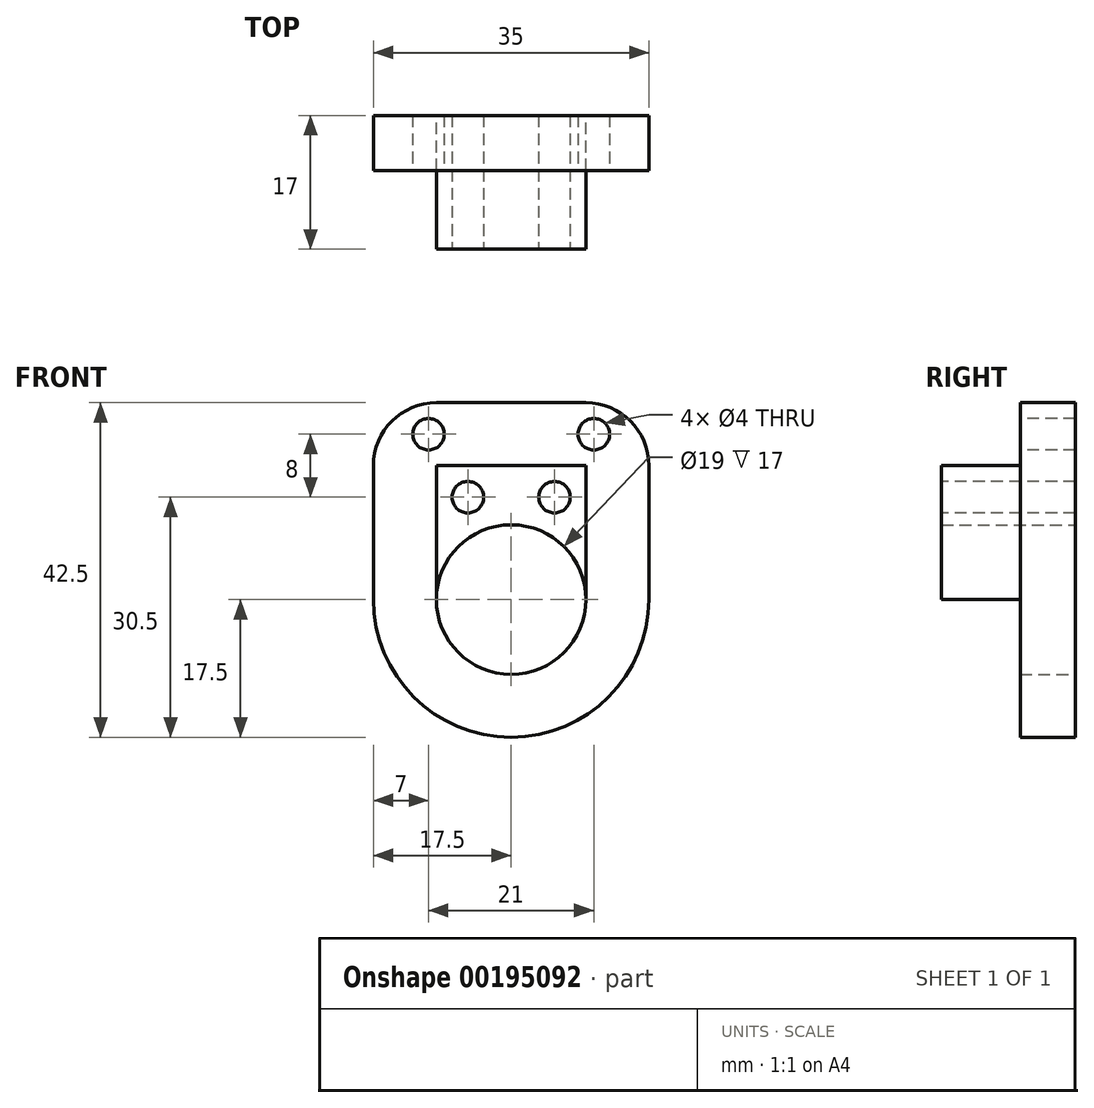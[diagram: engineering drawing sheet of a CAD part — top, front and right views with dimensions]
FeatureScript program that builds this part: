
annotation { "Feature Type Name" : "Feature", "Feature Type Description" : "" }
export const myFeature = defineFeature(function(context is Context, id is Id, definition is map)
    precondition{}
    {
        {
            var Q0;
            Q0=qCreatedBy(makeId("Front.planeOp"),FACE);
            var sketch = newSketch(context, id + "F0", { "sketchPlane" : qUnion([Q0])});
            skCircle(sketch, "E0", {"center": v(0, 0) * mm, "radius": 9.5 * mm});
            skArc(sketch, "E1", {"start": v(-17.5, 0) * mm, "mid": v(0, -17.5) * mm, "end": v(17.5, 0) * mm});
            skLineSegment(sketch, "E2", {"start": v(17.5, 0) * mm, "end": v(17.5, 25) * mm});
            skLineSegment(sketch, "E3", {"start": v(17.5, 25) * mm, "end": v(-17.5, 25) * mm});
            skLineSegment(sketch, "E4", {"start": v(-17.5, 25) * mm, "end": v(-17.5, 0) * mm});
            skSolve(sketch);
        }
        {
            var Q0;
            Q0 = qSketchRegion(id + "F0", true);
            extrude(context, id + "F1", {"entities" : qUnion([Q0]), "depth" : 7 * mm});
        }
        {
            var Q0;
            Q0=makeQuery(id+"F1.opExtrude","CAP_FACE",FACE,{"disambiguationData":[OSD([sQuery(id+"F0.wireOp",EDGE,"E0"),sQuery(id+"F0.wireOp",EDGE,"E1"),sQuery(id+"F0.wireOp",EDGE,"E2"),sQuery(id+"F0.wireOp",EDGE,"E3"),sQuery(id+"F0.wireOp",EDGE,"E4")])],"isStart":false});
            var sketch = newSketch(context, id + "F2", { "sketchPlane" : qUnion([Q0])});
            skArc(sketch, "E5.0", {"start": v(9.5, 0) * mm, "mid": v(0, 9.5) * mm, "end": v(-9.5, 0) * mm});
            skLineSegment(sketch, "E6", {"start": v(9.5, 0) * mm, "end": v(9.5, 17) * mm});
            skLineSegment(sketch, "E7", {"start": v(-9.5, 17) * mm, "end": v(-9.5, 0) * mm});
            skLineSegment(sketch, "E8", {"start": v(9.5, 17) * mm, "end": v(-9.5, 17) * mm});
            skSolve(sketch);
        }
        {
            var Q0;
            Q0 = qSketchRegion(id + "F2", true);
            extrude(context, id + "F3", {"entities" : qUnion([Q0]), "operationType" : NewBodyOperationType.ADD, "depth" : 10 * mm});
        }
        {
            var Q0;
            Q0=makeQuery(id+"F1.opExtrude","CAP_FACE",FACE,{"disambiguationData":[OSD([sQuery(id+"F0.wireOp",EDGE,"E0"),sQuery(id+"F0.wireOp",EDGE,"E1"),sQuery(id+"F0.wireOp",EDGE,"E2"),sQuery(id+"F0.wireOp",EDGE,"E3"),sQuery(id+"F0.wireOp",EDGE,"E4")])],"isStart":false});
            var sketch = newSketch(context, id + "F4", { "sketchPlane" : qUnion([Q0])});
            skPoint(sketch, "E9", {"position": v(-10.5, 21) * mm});
            skPoint(sketch, "E10", {"position": v(10.5, 21) * mm});
            skSolve(sketch);
        }
        {
            var Q0;
            Q0=sQuery(id+"F4.wireOp",VERTEX,"E9");
            var Q1;
            Q1=sQuery(id+"F4.wireOp",VERTEX,"E10");
            var Q2;
            Q2=makeQuery(id+"F1.opExtrude","SWEPT_BODY",BODY,{"disambiguationData":[OSD([sQuery(id+"F0.wireOp",EDGE,"E0"),sQuery(id+"F0.wireOp",EDGE,"E1"),sQuery(id+"F0.wireOp",EDGE,"E2"),sQuery(id+"F0.wireOp",EDGE,"E3"),sQuery(id+"F0.wireOp",EDGE,"E4")])]});
            hole(context, id + "F5", {"style" : HoleStyle.SIMPLE, "endStyle" : HoleEndStyle.BLIND, "holeDiameter" : 4 * mm, "holeDepth" : 10 * mm, "locations" : qUnion([Q0, Q1]), "scope" : qUnion([Q2])});
        }
        {
            var Q0;
            Q0=makeQuery(id+"F3.opExtrude","CAP_FACE",FACE,{"disambiguationData":[OSD([sQuery(id+"F2.wireOp",EDGE,"E5.0"),sQuery(id+"F2.wireOp",EDGE,"E6"),sQuery(id+"F2.wireOp",EDGE,"E7"),sQuery(id+"F2.wireOp",EDGE,"E8")])],"isStart":false});
            var sketch = newSketch(context, id + "F6", { "sketchPlane" : qUnion([Q0])});
            skPoint(sketch, "E11", {"position": v(-5.5, 13) * mm});
            skPoint(sketch, "E12", {"position": v(5.5, 13) * mm});
            skLineSegment(sketch, "E13", {"start": v(0, 17) * mm, "end": v(0, 3.41) * mm, "construction": true});
            skPoint(sketch, "E13.endSnap0", {"position": v(0, 9.5) * mm});
            skSolve(sketch);
        }
        {
            var Q0;
            Q0=sQuery(id+"F6.wireOp",VERTEX,"E11");
            var Q1;
            Q1=sQuery(id+"F6.wireOp",VERTEX,"E12");
            var Q2;
            Q2=makeQuery(id+"F1.opExtrude","SWEPT_BODY",BODY,{"disambiguationData":[OSD([sQuery(id+"F0.wireOp",EDGE,"E0"),sQuery(id+"F0.wireOp",EDGE,"E1"),sQuery(id+"F0.wireOp",EDGE,"E2"),sQuery(id+"F0.wireOp",EDGE,"E3"),sQuery(id+"F0.wireOp",EDGE,"E4")])]});
            hole(context, id + "F7", {"style" : HoleStyle.SIMPLE, "endStyle" : HoleEndStyle.THROUGH, "holeDiameter" : 4 * mm, "locations" : qUnion([Q0, Q1]), "scope" : qUnion([Q2]), "isTappedThrough" : true});
        }
        {
            var Q0;
            Q0=makeQuery(id+"F1.opExtrude","SWEPT_EDGE",EDGE,{"disambiguationData":[OSD([sQuery(id+"F0.wireOp",EDGE,"E3"),sQuery(id+"F0.wireOp",EDGE,"E4")])]});
            var Q1;
            Q1=makeQuery(id+"F1.opExtrude","SWEPT_EDGE",EDGE,{"disambiguationData":[OSD([sQuery(id+"F0.wireOp",EDGE,"E2"),sQuery(id+"F0.wireOp",EDGE,"E3")])]});
            fillet(context, id + "F8", {"entities" : qUnion([Q0, Q1]), "radius" : 8 * mm, "tangentPropagation" : true, "allowEdgeOverflow" : false});
        }
    });
